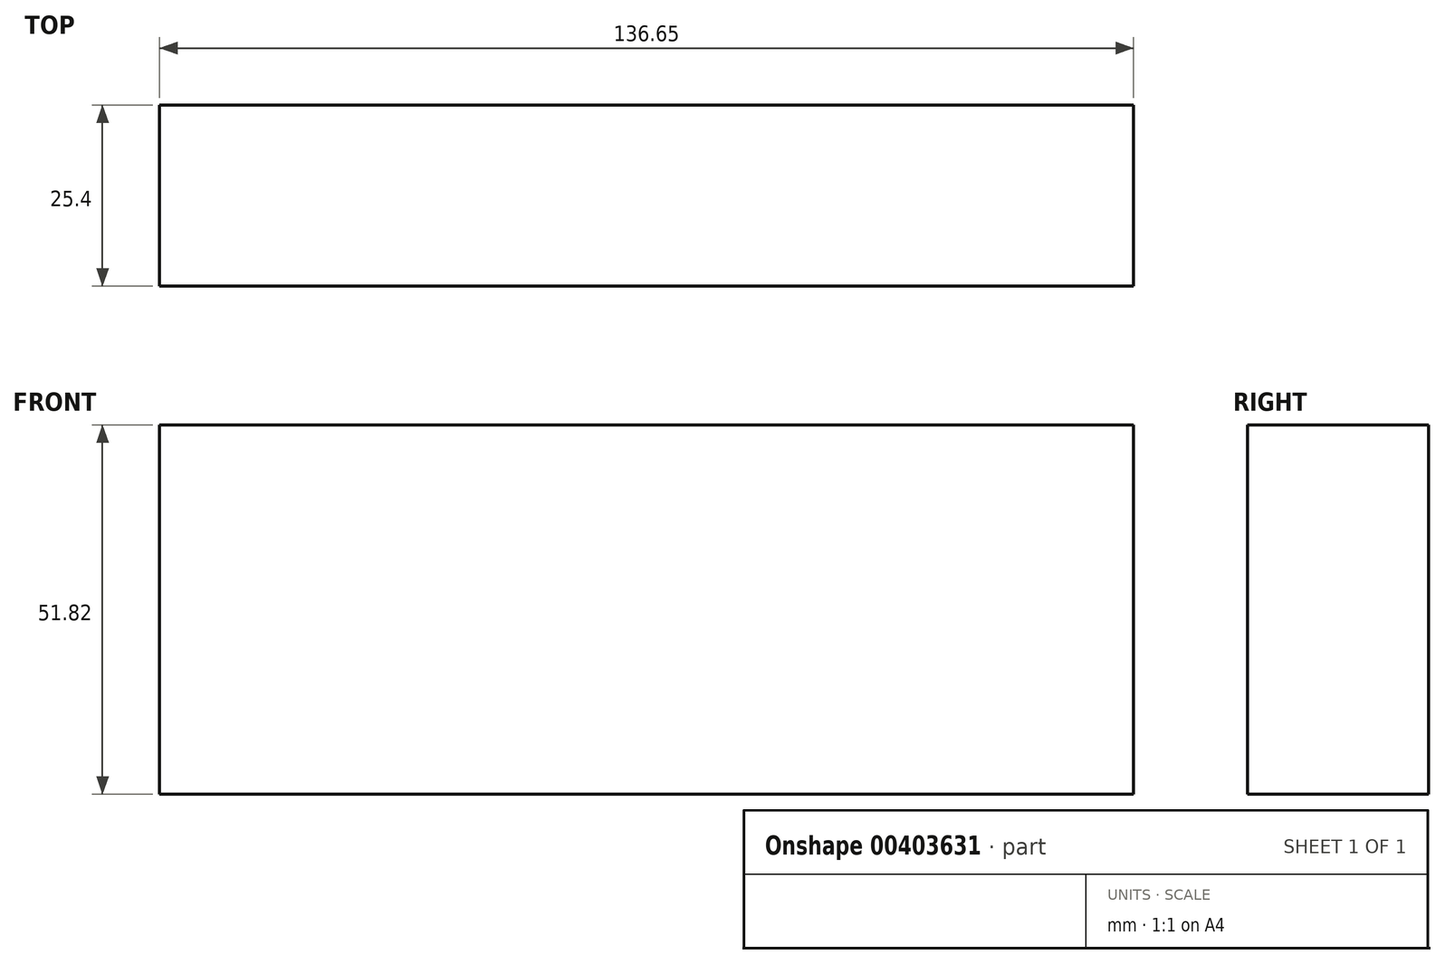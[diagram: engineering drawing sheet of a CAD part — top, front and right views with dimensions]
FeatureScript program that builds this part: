
annotation { "Feature Type Name" : "Feature", "Feature Type Description" : "" }
export const myFeature = defineFeature(function(context is Context, id is Id, definition is map)
    precondition{}
    {
        {
            var Q0;
            Q0=qCreatedBy(makeId("Front.planeOp"),FACE);
            var sketch = newSketch(context, id + "F0", { "sketchPlane" : qUnion([Q0])});
            skLineSegment(sketch, "E0.bottom", {"start": v(97.47, 60.32) * mm, "end": v(-39.18, 60.32) * mm});
            skLineSegment(sketch, "E0.top", {"start": v(97.47, 112.14) * mm, "end": v(-39.18, 112.14) * mm});
            skLineSegment(sketch, "E0.left", {"start": v(97.47, 60.32) * mm, "end": v(97.47, 112.14) * mm});
            skLineSegment(sketch, "E0.right", {"start": v(-39.18, 60.32) * mm, "end": v(-39.18, 112.14) * mm});
            skSolve(sketch);
        }
        {
            var Q0;
            Q0=makeQuery(id+"F0.imprint","IMPRINT",FACE,{"disambiguationData":[TD([[makeQuery(id+"F0.imprint","IMPRINT",EDGE,{"derivedFrom":sQuery(id+"F0.wireOp",EDGE,"E0.bottom")}),-1.0]])]});
            extrude(context, id + "F1", {"entities" : qUnion([Q0]), "depth" : 25.4 * mm});
        }
    });
